# Revit family: НЕВАТОМ_Нaгреватель NWPk, Версия 2
name_source: partatom
category: Оборудование
revit_build: Autodesk Revit 2017 (Build: 20170118_1100(x64)
units: mm (PartAtom-declared; Revit-internal decimal feet)

## family parameters
Всегда вертикально = Да
На основе рабочей плоскости = Нет
Общий = Нет
При загрузке вырезать с полостями = Нет
Размер круглого соединителя = Использовать диаметр
Тип детали = Вставляется
Точка расчета площади = Нет

## types (8) — shared parameters
ADSK_Единица измерения = шт.
ADSK_Завод-изготовитель = НЕВАТОМ
ADSK_Количество = 1
Nevatom_URL = https://t.me
Ключевая пометка = Вентиляция
Материал = Сталь серая
НЕВАТОМ_Температура воды на входе в нагреватель = 90 °C
НЕВАТОМ_Температура воды на выходе из нагревателя = 70 °C
Нипель = СВМПЭ, черный

## per-type parameters (varying)
| type | A | ADSK_Масса | ADSK_Полная мощность | ADSK_Потеря давления воздуха | ADSK_Размер_Высота | ADSK_Размер_Длина | ADSK_Размер_Ширина | ADSK_Расход воздуха | ADSK_Расход жидкости | B | C | D | E | F | K | L | M | c | c2 | d | НЕВАТОМ_Нагреватель расход воды | НЕВАТОМ_Узел регулирования нагревателя |
| NWPk-160/2 | 273 мм | 4.17 | 5 кВт | 40.0 Па | 203 мм | 375 мм | 316 мм | 290.0 м³/ч | 0.2 л/с | 203 мм | 162 мм | 160 мм | 316 мм | 375 мм | 316 мм | 210 мм | 24 мм | 24 мм | 65 мм | 15 мм | 0.2 м³/ч | "SUnw3 40–2,5/SUnw3 40–2,5pr" |
| NWPk-315/3 | 346 мм | 8.46 | 21 кВт | 82.0 Па | 346 мм | 430 мм | 266 мм | 1120.0 м³/ч | 1.0 л/с | 346 мм | 80 мм | 315 мм | 380 мм | 430 мм | 266 мм | 160 мм | 65 мм | 12 мм | 32 мм | 25 мм | 1.2 м³/ч | "SUnw3 40–2,5/SUnw3 40–2,5pr" |
| NWPk-315/2 | 423 мм | 8 | 17 кВт | 40.0 Па | 353 мм | 525 мм | 316 мм | 1120.0 м³/ч | 0.7 л/с | 353 мм | 312 мм | 315 мм | 466 мм | 525 мм | 316 мм | 210 мм | 24 мм | 47 мм | 125 мм | 15 мм | 0.9 м³/ч | "SUnw3 40–4,0/SUnw3 40–4,0pr" |
| NWPk-160/3 | 246 мм | 4.4 | 6 кВт | 82.0 Па | 246 мм | 280 мм | 266 мм | 290.0 м³/ч | 0.3 л/с | 246 мм | 80 мм | 160 мм | 275 мм | 280 мм | 266 мм | 160 мм | 65 мм | 12 мм | 32 мм | 25 мм | 0.3 м³/ч | "SUnw3 40–2,5/SUnw3 40–2,5pr" |
| NWPk-200/2 | 298 мм | 4.8 | 7 кВт | 40.0 Па | 228 мм | 400 мм | 316 мм | 450.0 м³/ч | 0.3 л/с | 228 мм | 187 мм | 200 мм | 341 мм | 400 мм | 316 мм | 210 мм | 24 мм | 28 мм | 75 мм | 15 мм | 0.4 м³/ч | "SUnw3 40–2,5/SUnw3 40–2,5pr" |
| NWPk-200/3 | 246 мм | 5.06 | 9 кВт | 82.0 Па | 246 мм | 330 мм | 266 мм | 450.0 м³/ч | 0.4 л/с | 246 мм | 80 мм | 200 мм | 280 мм | 330 мм | 266 мм | 160 мм | 65 мм | 12 мм | 32 мм | 25 мм | 0.5 м³/ч | "SUnw3 40–2,5/SUnw3 40–2,5pr" |
| NWPk-250/2 | 348 мм | 5.92 | 13 кВт | 40.0 Па | 278 мм | 450 мм | 316 мм | 700.0 м³/ч | 0.6 л/с | 278 мм | 237 мм | 250 мм | 391 мм | 450 мм | 316 мм | 210 мм | 24 мм | 36 мм | 95 мм | 15 мм | 0.6 м³/ч | "SUnw3 40–2,5/SUnw3 40–2,5pr" |
| NWPk-250/3 | 348 мм | 6.25 | 16 кВт | 82.0 Па | 348 мм | 380 мм | 266 мм | 700.0 м³/ч | 0.7 л/с | 348 мм | 80 мм | 250 мм | 330 мм | 380 мм | 266 мм | 160 мм | 65 мм | 12 мм | 32 мм | 25 мм | 0.8 м³/ч | "SUnw3 40–2,5/SUnw3 40–2,5pr" |
